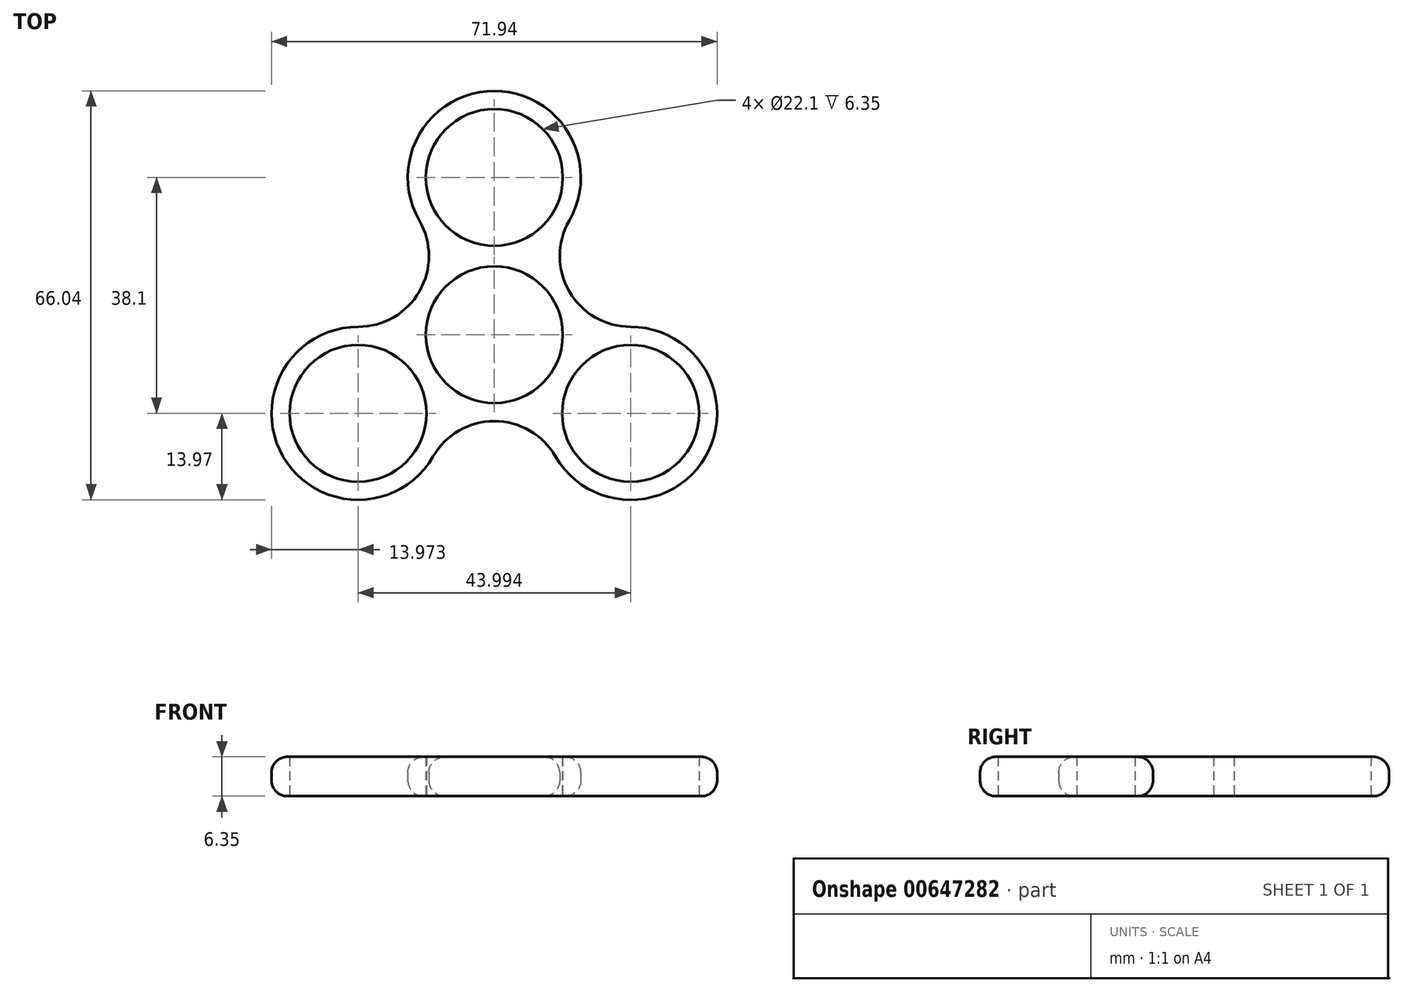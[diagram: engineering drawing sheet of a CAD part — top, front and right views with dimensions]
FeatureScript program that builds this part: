
annotation { "Feature Type Name" : "Feature", "Feature Type Description" : "" }
export const myFeature = defineFeature(function(context is Context, id is Id, definition is map)
    precondition{}
    {
        {
            var Q0;
            Q0=qCreatedBy(makeId("Top.planeOp"),FACE);
            var sketch = newSketch(context, id + "F0", { "sketchPlane" : qUnion([Q0])});
            skCircle(sketch, "E0", {"center": v(0, 0) * mm, "radius": 11.05 * mm});
            skArc(sketch, "E1", {"start": v(-25.39, 0.85) * mm, "mid": v(-25.4, -0.65) * mm, "end": v(-25.3, -2.16) * mm});
            skCircle(sketch, "E2", {"center": v(0, 25.4) * mm, "radius": 11.05 * mm});
            skCircle(sketch, "E3", {"center": v(0, 25.4) * mm, "radius": 13.97 * mm});
            skCircle(sketch, "E4.1.0", {"center": v(-22, -12.7) * mm, "radius": 13.97 * mm});
            skCircle(sketch, "E4.1.1", {"center": v(-22, -12.7) * mm, "radius": 11.05 * mm});
            skCircle(sketch, "E4.2.0", {"center": v(22, -12.7) * mm, "radius": 13.97 * mm});
            skCircle(sketch, "E4.2.1", {"center": v(22, -12.7) * mm, "radius": 11.05 * mm});
            skLineSegment(sketch, "E5", {"start": v(0, 11.05) * mm, "end": v(0, 11.43) * mm});
            skArc(sketch, "E6", {"start": v(-22, 1.27) * mm, "mid": v(-12.1, 6.99) * mm, "end": v(-12.1, 18.41) * mm});
            skArc(sketch, "E7.1.0", {"start": v(9.9, -19.69) * mm, "mid": v(0, -13.97) * mm, "end": v(-9.9, -19.69) * mm});
            skArc(sketch, "E7.2.0", {"start": v(12.1, 18.42) * mm, "mid": v(12.1, 6.99) * mm, "end": v(22, 1.27) * mm});
            skArc(sketch, "E8.trimOffspring", {"start": v(13.43, 21.56) * mm, "mid": v(12.13, 22.32) * mm, "end": v(10.78, 23) * mm});
            skArc(sketch, "E9.trimOffspring", {"start": v(25.3, -2.16) * mm, "mid": v(25.4, -0.65) * mm, "end": v(25.39, 0.85) * mm});
            skArc(sketch, "E10.trimOffspring", {"start": v(11.95, -22.41) * mm, "mid": v(13.26, -21.66) * mm, "end": v(14.52, -20.84) * mm});
            skArc(sketch, "E11.trimOffspring", {"start": v(-14.52, -20.84) * mm, "mid": v(-13.26, -21.66) * mm, "end": v(-11.95, -22.41) * mm});
            skArc(sketch, "E12.trimOffspring", {"start": v(-10.78, 23) * mm, "mid": v(-12.13, 22.32) * mm, "end": v(-13.43, 21.56) * mm});
            skSolve(sketch);
        }
        {
            var Q0;
            Q0=qSketchRegion(id+"F0",true);
            extrude(context, id + "F1", {"entities" : qUnion([Q0]), "depth" : 6.35 * mm, "offsetDistance" : 25.4 * mm});
        }
        {
            var Q0;
            Q0=makeQuery(id+"F1.opExtrude","CAP_EDGE",EDGE,{"disambiguationData":[OSD([sQuery(id+"F0.wireOp",EDGE,"E6")])],"isStart":false});
            var Q1;
            Q1=makeQuery(id+"F1.opExtrude","CAP_EDGE",EDGE,{"disambiguationData":[OSD([sQuery(id+"F0.wireOp",EDGE,"E7.1.0")])],"isStart":true});
            fillet(context, id + "F2", {"entities" : qUnion([Q0, Q1]), "radius" : 2.54 * mm, "tangentPropagation" : true, "allowEdgeOverflow" : false});
        }
    });
